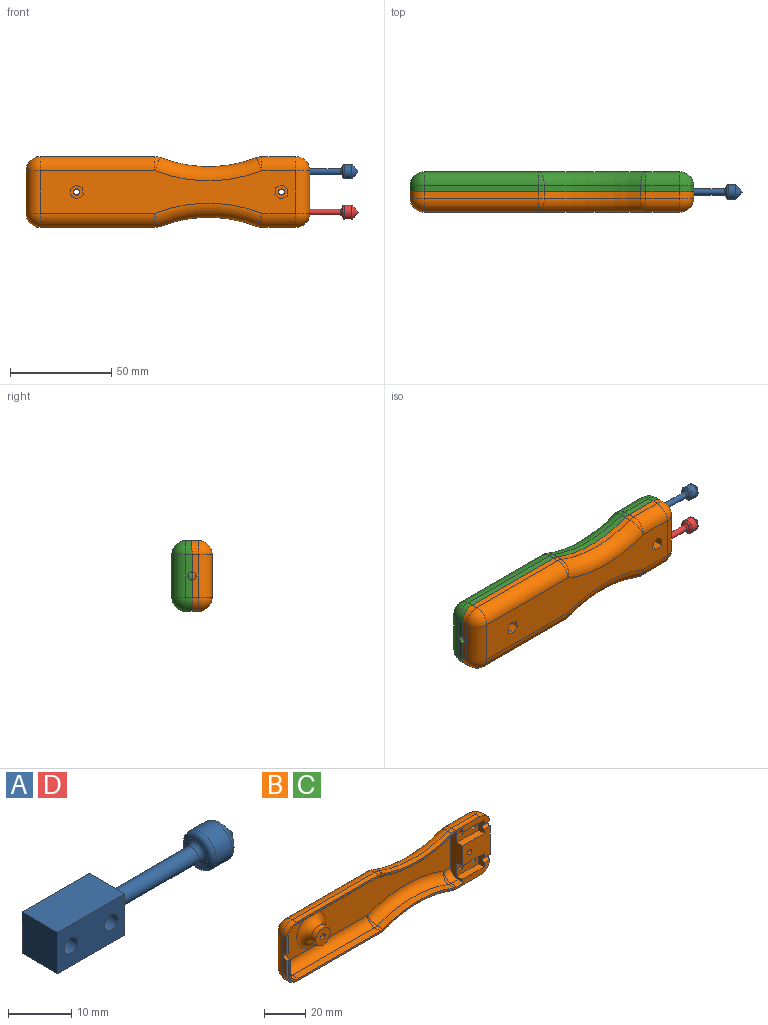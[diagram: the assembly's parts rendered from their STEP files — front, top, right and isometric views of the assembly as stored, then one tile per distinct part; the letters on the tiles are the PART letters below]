
ASSEMBLY  parts=4 mates=3
PART A: 15 faces, bbox 42.8x8x8 mm
  f0: sphere r=0.63mm, area 0.6mm2, adj f1
  f1: cone r=3.5mm half-angle=49.4deg, axis (-1,0,0), area 40.4mm2, adj f0,f12
  f2: cylinder r=3.5mm len=7mm, axis (1,0,0), area 77.9mm2, adj f12,f14
  f3: cylinder r=1.5mm len=19mm, axis (1,0,0), area 179.1mm2, adj f4,f13
  f4: plane 8x8mm, normal (1,0,0), area 56.9mm2, adj f3,f5,f6,f7,f8
  f5: plane 15x8mm, normal (0,0,1), area 120mm2, adj f4,f6,f7,f9
  f6: plane 15x8mm, normal (0,-1,0), area 105.9mm2, adj f4,f5,f8,f9,f10,f11
  f7: plane 15x8mm, normal (0,1,0), area 105.9mm2, adj f4,f5,f8,f9,f10,f11
  f8: plane 15x8mm, normal (0,0,-1), area 120mm2, adj f4,f6,f7,f9
  f9: plane 8x8mm, normal (-1,0,0), area 64mm2, adj f5,f6,f7,f8
  f10: cylinder r=1.5mm len=8mm, axis (0,-1,0), area 75.4mm2, adj f6,f7
  f11: cylinder r=1.5mm len=8mm, axis (0,-1,0), area 75.4mm2, adj f6,f7
  f12: torus R=2.5mm, axis (-1,0,0), area 18.3mm2, adj f1,f2
  f13: torus R=2.5mm, axis (1,0,0), area 18.4mm2, adj f3,f14
  f14: torus R=2.5mm, axis (1,0,0), area 31mm2, adj f2,f13
PART B: 141 faces, bbox 140x12x35 mm
  f0: plane 56.63x2mm, normal (0,0,-1), area 113.3mm2, adj f2,f3,f94,f140
  f1: cylinder r=5mm len=2mm, axis (0,-1,0), area 3.8mm2, adj f23,f24,f86,f140
  f2: cylinder r=5mm len=2mm, axis (0,-1,0), area 3.8mm2, adj f0,f24,f91,f140
  f3: cylinder r=5mm len=5mm, axis (0,1,0), area 15.7mm2, adj f0,f6,f96,f140
  f4: plane 139.93x15.5mm, normal (0,-1,0), area 200mm2, adj f5,f9,f12,f15,f16,f20,f44,f79
  f5: plane 21x3mm, normal (-1,0,0), area 56.7mm2, adj f4,f7,f80,f103,f108,f109
  f6: plane 21x4mm, normal (1,0,0), area 56.7mm2, adj f3,f80,f93,f97,f122,f131,f134,f140
  f7: plane 139.93x15.5mm, normal (0,-1,0), area 200mm2, adj f5,f10,f12,f17,f18,f19,f47,f78
  f8: plane 21x3mm, normal (1,0,0), area 58mm2, adj f11,f78,f79,f106,f112,f113
  f9: plane 8x4mm, normal (-1,0,0), area 28.5mm2, adj f4,f11,f44,f45,f46,f79
  f10: plane 8x4mm, normal (-1,0,0), area 28.5mm2, adj f7,f11,f47,f48,f49,f78
  f11: plane 19x17mm, normal (0,-1,0), area 240.9mm2, adj f8,f9,f10,f12,f14,f45,f48,f78
  f12: plane 32x8mm, normal (-1,0,0), area 174.3mm2, adj f4,f7,f11,f22,f23,f27,f44,f45
  f13: cylinder r=1.5mm len=5mm, axis (0,-1,0), area 47.1mm2, adj f28,f37
  f14: cylinder r=1.5mm len=5mm, axis (0,-1,0), area 47.1mm2, adj f11,f30
  f15: cylinder r=64.85mm len=47.6mm, axis (0,1,0), area 146.2mm2, adj f4,f115,f119,f121
  f16: plane 16.63x3mm, normal (0,0,-1), area 49.9mm2, adj f4,f112,f118,f121
  f17: plane 16.63x3mm, normal (0,0,1), area 49.9mm2, adj f7,f100,f106,f107
  f18: cylinder r=64.85mm len=47.6mm, axis (0,1,0), area 146.2mm2, adj f7,f98,f100,f101
  f19: plane 56.63x3mm, normal (0,0,1), area 169.9mm2, adj f7,f98,f102,f103
  f20: plane 56.63x3mm, normal (0,0,-1), area 169.9mm2, adj f4,f109,f114,f115
  f21: plane 126x21mm, normal (0,1,0), area 2228.7mm2, adj f31,f32,f33,f34,f35,f36,f38,f39
  f22: plane 114x21mm, normal (0,-1,0), area 1724.9mm2, adj f12,f81,f82,f84,f87,f89,f92,f94
  f23: plane 4.63x2mm, normal (0,0,-1), area 9.3mm2, adj f1,f12,f84,f140
  f24: cylinder r=66.85mm len=49.06mm, axis (0,-1,0), area 100.5mm2, adj f1,f2,f89,f140
  f25: plane 56.63x4mm, normal (0,0,1), area 226.5mm2, adj f88,f92,f93,f131
  f26: cylinder r=66.85mm len=49.06mm, axis (0,-1,0), area 200.9mm2, adj f83,f87,f88,f131
  f27: plane 4.63x4mm, normal (0,0,1), area 18.5mm2, adj f12,f82,f83,f130,f131
  f28: plane 10x10mm, normal (0,-1,0), area 71.5mm2, adj f13,f29
  f29: cylinder r=5mm len=10mm, axis (0,1,0), area 94.2mm2, adj f28,f81
  f30: plane 6.88x6.36mm, normal (0,1,0), area 24.1mm2, adj f14,f31,f32,f33,f34,f35,f36
  f31: plane 5x3.44mm, normal (0.99,0,0.11), area 17.3mm2, adj f21,f30,f32,f36
  f32: plane 5x2.78mm, normal (0.6,0,-0.8), area 17.3mm2, adj f21,f30,f31,f33
  f33: plane 5x3.18mm, normal (-0.4,0,-0.92), area 17.3mm2, adj f21,f30,f32,f34
  f34: plane 5x3.44mm, normal (-0.99,0,-0.11), area 17.3mm2, adj f21,f30,f33,f35
  f35: plane 5x2.78mm, normal (-0.6,0,0.8), area 17.3mm2, adj f21,f30,f34,f36
  f36: plane 5x3.18mm, normal (0.4,0,0.92), area 17.3mm2, adj f21,f30,f31,f35
  f37: plane 6.81x6.53mm, normal (0,1,0), area 24.1mm2, adj f13,f38,f39,f40,f41,f42,f43
  f38: plane 5x3.26mm, normal (0.33,0,-0.94), area 17.3mm2, adj f21,f37,f39,f43
  f39: plane 5x2.64mm, normal (-0.65,0,-0.76), area 17.3mm2, adj f21,f37,f38,f40
  f40: plane 5x3.41mm, normal (-0.98,0,0.18), area 17.3mm2, adj f21,f37,f39,f41
  f41: plane 5x3.26mm, normal (-0.33,0,0.94), area 17.3mm2, adj f21,f37,f40,f42
  f42: plane 5x2.64mm, normal (0.65,0,0.76), area 17.3mm2, adj f21,f37,f41,f43
  f43: plane 5x3.41mm, normal (0.98,0,-0.18), area 17.3mm2, adj f21,f37,f38,f42
  f44: plane 15x4mm, normal (0,0,1), area 60mm2, adj f4,f9,f12,f46
  f45: plane 15x4mm, normal (0,0,-1), area 60mm2, adj f9,f11,f12,f46
  f46: plane 15x8mm, normal (0,-1,0), area 104.4mm2, adj f9,f12,f44,f45,f65,f66,f67,f68
  f47: plane 15x4mm, normal (0,0,-1), area 60mm2, adj f7,f10,f12,f49
  f48: plane 15x4mm, normal (0,0,1), area 60mm2, adj f10,f11,f12,f49
  f49: plane 15x8mm, normal (0,-1,0), area 104.4mm2, adj f10,f12,f47,f48,f51,f52,f53,f54
  f50: plane 3.46x3mm, normal (0,-1,0), area 7.8mm2, adj f51,f52,f53,f54,f55,f56
  f51: plane 4x1.73mm, normal (0,0,1), area 6.9mm2, adj f49,f50,f52,f56
  f52: plane 4x1.5mm, normal (-0.87,0,0.5), area 6.9mm2, adj f49,f50,f51,f53
  f53: plane 4x1.5mm, normal (-0.87,0,-0.5), area 6.9mm2, adj f49,f50,f52,f54
  f54: plane 4x1.73mm, normal (0,0,-1), area 6.9mm2, adj f49,f50,f53,f55
  f55: plane 4x1.5mm, normal (0.87,0,-0.5), area 6.9mm2, adj f49,f50,f54,f56
  f56: plane 4x1.5mm, normal (0.87,0,0.5), area 6.9mm2, adj f49,f50,f51,f55
  f57: plane 3.46x3mm, normal (0,-1,0), area 7.8mm2, adj f58,f59,f60,f61,f62,f63
  f58: plane 4x1.73mm, normal (0,0,1), area 6.9mm2, adj f49,f57,f59,f63
  f59: plane 4x1.5mm, normal (-0.87,0,0.5), area 6.9mm2, adj f49,f57,f58,f60
  f60: plane 4x1.5mm, normal (-0.87,0,-0.5), area 6.9mm2, adj f49,f57,f59,f61
  f61: plane 4x1.73mm, normal (0,0,-1), area 6.9mm2, adj f49,f57,f60,f62
  f62: plane 4x1.5mm, normal (0.87,0,-0.5), area 6.9mm2, adj f49,f57,f61,f63
  f63: plane 4x1.5mm, normal (0.87,0,0.5), area 6.9mm2, adj f49,f57,f58,f62
  f64: plane 3.46x3mm, normal (0,-1,0), area 7.8mm2, adj f65,f66,f67,f68,f69,f70
  f65: plane 4x1.73mm, normal (0,0,-1), area 6.9mm2, adj f46,f64,f66,f68
  f66: plane 4x1.5mm, normal (0.87,0,-0.5), area 6.9mm2, adj f46,f64,f65,f67
  f67: plane 4x1.5mm, normal (0.87,0,0.5), area 6.9mm2, adj f46,f64,f66,f69
  f68: plane 4x1.5mm, normal (-0.87,0,-0.5), area 6.9mm2, adj f46,f64,f65,f70
  f69: plane 4x1.73mm, normal (0,0,1), area 6.9mm2, adj f46,f64,f67,f70
  f70: plane 4x1.5mm, normal (-0.87,0,0.5), area 6.9mm2, adj f46,f64,f68,f69
  f71: plane 3.46x3mm, normal (0,-1,0), area 7.8mm2, adj f72,f73,f74,f75,f76,f77
  f72: plane 4x1.5mm, normal (0.87,0,0.5), area 6.9mm2, adj f46,f71,f73,f75
  f73: plane 4x1.73mm, normal (0,0,1), area 6.9mm2, adj f46,f71,f72,f74
  f74: plane 4x1.5mm, normal (-0.87,0,0.5), area 6.9mm2, adj f46,f71,f73,f76
  f75: plane 4x1.5mm, normal (0.87,0,-0.5), area 6.9mm2, adj f46,f71,f72,f77
  f76: plane 4x1.5mm, normal (-0.87,0,-0.5), area 6.9mm2, adj f46,f71,f74,f77
  f77: plane 4x1.73mm, normal (0,0,-1), area 6.9mm2, adj f46,f71,f75,f76
  f78: cylinder r=1.5mm len=4mm, axis (1,0,0), area 18.8mm2, adj f7,f8,f10,f11,f106
  f79: cylinder r=1.5mm len=4mm, axis (1,0,0), area 18.8mm2, adj f4,f8,f9,f11,f112
  f80: cylinder r=2mm len=4mm, axis (-1,0,0), area 12.6mm2, adj f4,f5,f6,f7,f122,f134
  f81: torus R=10mm, axis (0,-1,0), area 336.4mm2, adj f22,f29
  f82: cylinder r=5mm len=5mm, axis (-1,0,0), area 36.4mm2, adj f12,f22,f27,f85
  f83: cylinder r=5mm len=4mm, axis (0,-1,0), area 7.5mm2, adj f26,f27,f85,f131
  f84: cylinder r=5mm len=5mm, axis (1,0,0), area 36.4mm2, adj f12,f22,f23,f86
  f85: sphere r=5mm, area 9.4mm2, adj f82,f83,f87
  f86: sphere r=5mm, area 9.4mm2, adj f1,f84,f89
  f87: torus R=71.85mm, axis (0,-1,0), area 405.3mm2, adj f22,f26,f85,f90
  f88: cylinder r=5mm len=4mm, axis (0,-1,0), area 7.5mm2, adj f25,f26,f90,f131
  f89: torus R=71.85mm, axis (0,-1,0), area 405.3mm2, adj f22,f24,f86,f91
  f90: sphere r=5mm, area 9.4mm2, adj f87,f88,f92
  f91: sphere r=5mm, area 9.4mm2, adj f2,f89,f94
  f92: cylinder r=5mm len=56.63mm, axis (-1,0,0), area 444.8mm2, adj f22,f25,f90,f95
  f93: cylinder r=5mm len=5mm, axis (0,-1,0), area 31.4mm2, adj f6,f25,f95,f131
  f94: cylinder r=5mm len=56.63mm, axis (1,0,0), area 444.8mm2, adj f0,f22,f91,f96
  f95: sphere r=5mm, area 39.3mm2, adj f92,f93,f97
  f96: sphere r=5mm, area 39.3mm2, adj f3,f94,f97
  f97: cylinder r=5mm len=21mm, axis (0,0,1), area 164.9mm2, adj f6,f22,f95,f96
  f98: cylinder r=7mm len=3mm, axis (0,1,0), area 7.9mm2, adj f7,f18,f19,f99
  f99: sphere r=7mm, area 18.4mm2, adj f98,f101,f102
  f100: cylinder r=7mm len=3mm, axis (0,1,0), area 7.9mm2, adj f7,f17,f18,f104
  f101: torus R=71.85mm, axis (0,-1,0), area 556.9mm2, adj f18,f21,f99,f104
  f102: cylinder r=7mm len=56.63mm, axis (-1,0,0), area 622.7mm2, adj f19,f21,f99,f105
  f103: cylinder r=7mm len=7mm, axis (0,1,0), area 33mm2, adj f5,f7,f19,f105
  f104: sphere r=7mm, area 18.4mm2, adj f100,f101,f107
  f105: sphere r=7mm, area 77mm2, adj f102,f103,f108
  f106: cylinder r=7mm len=7mm, axis (0,-1,0), area 32mm2, adj f7,f8,f17,f78,f110
  f107: cylinder r=7mm len=16.63mm, axis (-1,0,0), area 182.9mm2, adj f17,f21,f104,f110
  f108: cylinder r=7mm len=21mm, axis (0,0,-1), area 230.9mm2, adj f5,f21,f105,f111
  f109: cylinder r=7mm len=7mm, axis (0,-1,0), area 33mm2, adj f4,f5,f20,f111
  f110: sphere r=7mm, area 77mm2, adj f106,f107,f113
  f111: sphere r=7mm, area 77mm2, adj f108,f109,f114
  f112: cylinder r=7mm len=7mm, axis (0,1,0), area 32mm2, adj f4,f8,f16,f79,f116
  f113: cylinder r=7mm len=21mm, axis (0,0,1), area 230.9mm2, adj f8,f21,f110,f116
  f114: cylinder r=7mm len=56.63mm, axis (1,0,0), area 622.7mm2, adj f20,f21,f111,f117
  f115: cylinder r=7mm len=3mm, axis (0,1,0), area 7.9mm2, adj f4,f15,f20,f117
  f116: sphere r=7mm, area 77mm2, adj f112,f113,f118
  f117: sphere r=7mm, area 18.4mm2, adj f114,f115,f119
  f118: cylinder r=7mm len=16.63mm, axis (1,0,0), area 182.9mm2, adj f16,f21,f116,f120
  f119: torus R=71.85mm, axis (0,-1,0), area 556.9mm2, adj f15,f21,f117,f120
  f120: sphere r=7mm, area 18.4mm2, adj f118,f119,f121
  f121: cylinder r=7mm len=3mm, axis (0,1,0), area 7.9mm2, adj f4,f15,f16,f120
  f122: plane 1x1mm, normal (0,0,1), area 1mm2, adj f6,f80,f123,f131
  f123: plane 8.5x1mm, normal (-1,0,0), area 8.5mm2, adj f4,f122,f124,f131
  f124: cylinder r=6mm len=6mm, axis (0,1,0), area 9.4mm2, adj f4,f123,f125,f131
  f125: plane 56.63x1mm, normal (0,0,-1), area 56.6mm2, adj f4,f124,f126,f131
  f126: cylinder r=6mm len=2.2mm, axis (0,1,0), area 2.3mm2, adj f4,f125,f127,f131
  f127: cylinder r=65.85mm len=48.33mm, axis (0,1,0), area 49.5mm2, adj f4,f126,f128,f131
  f128: cylinder r=6mm len=2.2mm, axis (0,1,0), area 2.3mm2, adj f4,f127,f129,f131
  f129: plane 4.63x1mm, normal (0,0,-1), area 4.6mm2, adj f4,f128,f130,f131
  f130: plane 1x1mm, normal (1,0,0), area 1mm2, adj f4,f27,f129,f131
  f131: plane 120x14.5mm, normal (0,-1,0), area 132.4mm2, adj f6,f25,f26,f27,f83,f88,f93,f122
  f132: cylinder r=6mm len=6mm, axis (0,-1,0), area 9.4mm2, adj f7,f133,f139,f140
  f133: plane 8.5x1mm, normal (1,0,0), area 8.5mm2, adj f7,f132,f134,f140
  f134: plane 1x1mm, normal (0,0,1), area 1mm2, adj f6,f80,f133,f140
  f135: plane 4.63x1mm, normal (0,0,-1), area 4.6mm2, adj f7,f12,f136,f140
  f136: cylinder r=6mm len=2.2mm, axis (0,-1,0), area 2.3mm2, adj f7,f135,f137,f140
  f137: cylinder r=65.85mm len=48.33mm, axis (0,-1,0), area 49.5mm2, adj f7,f136,f138,f140
  f138: cylinder r=6mm len=2.2mm, axis (0,-1,0), area 2.3mm2, adj f7,f137,f139,f140
  f139: plane 56.63x1mm, normal (0,0,-1), area 56.6mm2, adj f7,f132,f138,f140
  f140: plane 120x14.5mm, normal (0,-1,0), area 132.4mm2, adj f0,f1,f2,f3,f6,f12,f23,f24
PART C: same geometry as B
PART D: same geometry as A
PLACE A rot(axis=(1,0,0),180deg) t=(11.6,1.97,25.13)mm
PLACE B rot(axis=(1,0,0),180deg) t=(-39.4,-8.03,15.13)mm
PLACE C t=(-39.4,11.97,15.13)mm
PLACE D rot(axis=(1,0,0),180deg) t=(11.6,1.97,5.13)mm
MATE fastened A.f6 <-> C.f49  axis (0,1,0) through (19.1,5.97,25.13)mm
MATE fastened D.f6 <-> C.f46  axis (0,1,0) through (19.1,5.97,5.13)mm
MATE fastened B.f11 <-> C.f11  axis (0,1,0) through (21.86,1.97,15.13)mm
